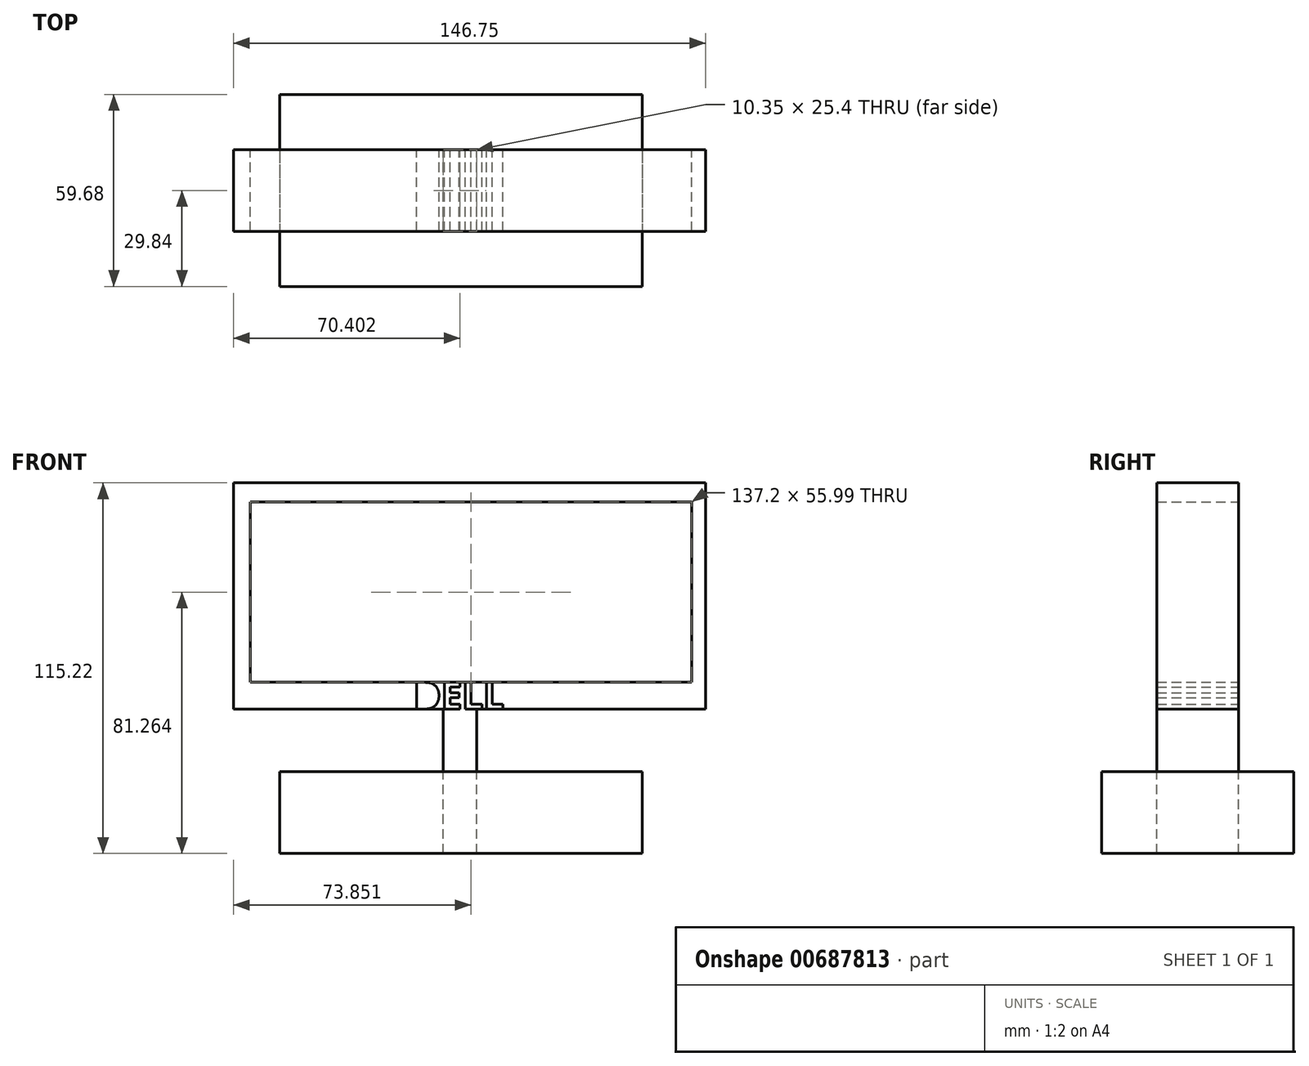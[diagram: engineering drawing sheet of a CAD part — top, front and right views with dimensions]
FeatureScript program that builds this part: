
annotation { "Feature Type Name" : "Feature", "Feature Type Description" : "" }
export const myFeature = defineFeature(function(context is Context, id is Id, definition is map)
    precondition{}
    {
        {
            var Q0;
            Q0=qCreatedBy(makeId("Front.planeOp"),FACE);
            var sketch = newSketch(context, id + "F0", { "sketchPlane" : qUnion([Q0])});
            skLineSegment(sketch, "E0", {"start": v(-68.6, 65.8) * mm, "end": v(76.03, 65.8) * mm});
            skLineSegment(sketch, "E1", {"start": v(76.03, 65.8) * mm, "end": v(76.03, -4.51) * mm});
            skLineSegment(sketch, "E2", {"start": v(76.03, -4.51) * mm, "end": v(-70.72, -4.51) * mm});
            skLineSegment(sketch, "E3", {"start": v(-70.72, -4.51) * mm, "end": v(-70.72, 65.8) * mm});
            skLineSegment(sketch, "E4", {"start": v(-70.72, 65.8) * mm, "end": v(-68.6, 65.8) * mm});
            skLineSegment(sketch, "E5", {"start": v(-70.72, 7.16) * mm, "end": v(-70.72, 11.14) * mm});
            skLineSegment(sketch, "E6", {"start": v(-65.47, 59.85) * mm, "end": v(-65.47, 3.86) * mm});
            skLineSegment(sketch, "E7", {"start": v(-65.47, 3.86) * mm, "end": v(68.55, 3.86) * mm});
            skLineSegment(sketch, "E8", {"start": v(68.55, 3.86) * mm, "end": v(71.73, 3.86) * mm});
            skLineSegment(sketch, "E9", {"start": v(71.73, 3.86) * mm, "end": v(71.73, 60.65) * mm});
            skLineSegment(sketch, "E10", {"start": v(-65.47, 59.85) * mm, "end": v(71.73, 59.85) * mm});
            skLineSegment(sketch, "E11", {"start": v(71.73, 59.85) * mm, "end": v(71.73, 3.86) * mm});
            skPoint(sketch, "E12.end.orphan", {"position": v(-8.36, -22.03) * mm});
            skPoint(sketch, "E12.start.orphan", {"position": v(6.24, -22.03) * mm});
            skLineSegment(sketch, "E13", {"start": v(-5.5, -4.51) * mm, "end": v(-5.5, -24) * mm});
            skLineSegment(sketch, "E14", {"start": v(4.86, -4.51) * mm, "end": v(4.86, -24) * mm});
            skLineSegment(sketch, "E15", {"start": v(-5.5, -24) * mm, "end": v(4.86, -24) * mm});
            skText(sketch, "E16", { "text": "DELL", "fontName": "OpenSans-Bold.ttf"});
            skLineSegment(sketch, "E17", {"start": v(-8.1, -4.51) * mm, "end": v(-14.78, -4.51) * mm});
            skLineSegment(sketch, "E18", {"start": v(-14.78, -4.51) * mm, "end": v(13.83, -4.51) * mm});
            const initialGuessF0  = {"E16": [-0.01478, -0.00451, 1, 0, 0.00837]};
            skSetInitialGuess(sketch, initialGuessF0);
            skSolve(sketch);
        }
        {
            var Q0;
            Q0=makeQuery(id+"F0.imprint","IMPRINT",FACE,{"disambiguationData":[TD([[makeQuery(id+"F0.imprint","IMPRINT",EDGE,{"derivedFrom":sQuery(id+"F0.wireOp",EDGE,"E0")}),-1.0]])]});
            var Q1;
            {var subQ1=sQuery(id+"F0.wireOp",EDGE,"E13");Q1=makeQuery(id+"F0.imprint","IMPRINT",FACE,{"disambiguationData":[TD([[makeQuery(id+"F0.imprint","IMPRINT",EDGE,{"derivedFrom":subQ1}),1.0]])]});}
            extrude(context, id + "F1", {"entities" : qUnion([Q0, Q1]), "depth" : 25.4 * mm, "offsetDistance" : 25.4 * mm});
        }
        {
            var Q0;
            Q0=makeQuery(id+"F1.opExtrude","SWEPT_FACE",FACE,{"disambiguationData":[OSD([sQuery(id+"F0.wireOp",EDGE,"E15")])]});
            var sketch = newSketch(context, id + "F2", { "sketchPlane" : qUnion([Q0])});
            skLineSegment(sketch, "E19.bottom", {"start": v(56.3, -17.14) * mm, "end": v(-56.3, -17.14) * mm});
            skLineSegment(sketch, "E19.top", {"start": v(56.3, 42.54) * mm, "end": v(-56.3, 42.54) * mm});
            skLineSegment(sketch, "E19.left", {"start": v(56.3, -17.14) * mm, "end": v(56.3, 42.54) * mm});
            skLineSegment(sketch, "E19.right", {"start": v(-56.3, -17.14) * mm, "end": v(-56.3, 42.54) * mm});
            skPoint(sketch, "E19.middle", {"position": v(0, 12.7) * mm});
            skPoint(sketch, "E19.middle.positionSnap0", {"position": v(-5.5, 12.7) * mm});
            skPoint(sketch, "E19.centerSnap0", {"position": v(-5.5, 12.7) * mm});
            skSolve(sketch);
        }
        {
            var Q0;
            Q0=makeQuery(id+"F2.imprint","IMPRINT",FACE,{"disambiguationData":[TD([[makeQuery(id+"F2.imprint","IMPRINT",EDGE,{"derivedFrom":sQuery(id+"F2.wireOp",EDGE,"E19.bottom")}),-1.0]])]});
            extrude(context, id + "F3", {"entities" : qUnion([Q0]), "depth" : 25.4 * mm, "offsetDistance" : 25.4 * mm});
        }
    });
